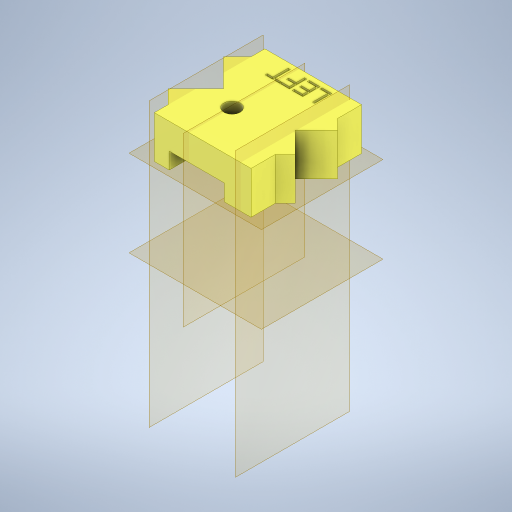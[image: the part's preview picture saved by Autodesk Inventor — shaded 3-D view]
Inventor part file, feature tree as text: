
AUTODESK INVENTOR PART (.ipt)
format: ipt  version: 2023 (Build 270158030, 158C)  size: 1,032,192 bytes
history: native  units: mm
features: sketch x32, extrude x26, projected_geometry x14, hole x7, plane x5, emboss x4, split x3, mirror x2
ambient origin geometry x8: Origin, YZ Plane, XZ Plane, XY Plane, X Axis, Y Axis, Z Axis, Center Point
bodies: Solid1 (feature_tree)
feature tree (93):
  extrude  "MainInnerBodyExtrusion"  Depth=149.0mm
  extrude  "HoleForCamerabase"  Depth=50.0mm
  extrude  "HoleForFan"  Depth=59.0mm
  extrude  "HoleForPi"  TaperAngle=0.0deg  [1 undecoded]
  extrude  "HoleForPoeAdapter"  Depth=62.0mm
  extrude  "HoleForThermister"  Depth=47.0mm
  extrude  "HoleForSensor"  Depth=32.0mm
  extrude  "SlotsForRearFan"  Depth=47.0mm
  extrude  "VentForCamera"  Depth=16.0mm
  extrude  "HoleForLens"  Depth=118.0mm
  sketch  "Sketch23"  dims[d26=49.0mm d27=118.0mm]
  hole  "Hole for 6-32 Insert"  [1 undecoded]
  hole  "Screw hole for 6-32 screw"  [1 undecoded]
  extrude  "Extrusion18"  TaperAngle=0.0deg  [1 undecoded]
  extrude  "HoleForPowerWire"  Depth=17.0mm
  extrude  "Extrusion22"  TaperAngle=0.0deg  [1 undecoded]
  extrude  "Extrusion23"  Depth=2.0mm
  extrude  "ExtrusionForBottom"  Depth=4.0mm
  sketch  "Sketch40"  dims[d46=31.5mm d47=0.0mm]
  plane  "Work Plane1"
  plane  "Work Plane2"
  extrude  "CutOutForFilter"  Depth=4.0mm
  hole  "Hole13"  [1 undecoded]
  plane  "Work Plane4"
  plane  "Work Plane5"
  split  "Split8"
  split  "Split9"
  extrude  "Extrusion35"  Depth=3.0mm
  extrude  "Extrusion36"  Depth=10.0mm
  extrude  "Extrusion37"  Depth=1.5mm
  extrude  "Extrusion38"  Depth=3.0mm
  extrude  "Extrusion to Fix Error"  TaperAngle=0.0deg  [1 undecoded]
  extrude  "Extrusion41"  Depth=15.0mm
  extrude  "Extrusion42"  Depth=5.0mm
  hole  "Hole17"  [1 undecoded]
  hole  "Hole18"  [1 undecoded]
  hole  "Hole19"  [1 undecoded]
  extrude  "Extrusion43"  Depth=1.0mm
  plane  "Work Plane6"
  extrude  "Extrusion44"  Depth=1.0mm
  emboss  "Emboss1"
  emboss  "Emboss2"
  emboss  "Emboss3"
  extrude  "Extrusion45"  Depth=1.0mm
  mirror  "Mirror5"
  hole  "Hole20"  [1 undecoded]
  emboss  "Emboss4"
  mirror  "Mirror6"
  split  "Split11"
  sketch  "Sketch1"  dims[d0=222.7mm d1=149.0mm]
  sketch  "Sketch3"  dims[d2=50.0mm d3=0.0mm d5=15.7mm]
  sketch  "Sketch4"  dims[d6=54.0mm d7=59.0mm]
  sketch  "Sketch6"  dims[d8=47.0mm d9=0.0mm]
  sketch  "Sketch7"  dims[d13=16.0mm d14=62.0mm]
  sketch  "Sketch11"  dims[d15=3.0mm d16=47.0mm]
  sketch  "Sketch15"  dims[d17=0.0mm d20=32.0mm]
  sketch  "Sketch16"  dims[d21=129.0mm d22=47.0mm]
  sketch  "Sketch18"  dims[d23=0.0mm d25=16.0mm]
  sketch  "Sketch25"  dims[d28=47.0mm d29=0.0mm]
  projected_geometry  "Projected Loop1"
  sketch  "Sketch26"  dims[d36=69.0mm d37=28.0mm]
  sketch  "Sketch37"  dims[d38=47.0mm d39=0.0mm]
  projected_geometry  "Projected Loop3"
  projected_geometry  "Projected Loop4"
  sketch  "Sketch39"  dims[d42=50.0mm d43=17.0mm]
  projected_geometry  "Projected Loop5"
  sketch  "Sketch43"  dims[d67=60.0mm d69=2.0mm]
  projected_geometry  "Projected Loop8"
  projected_geometry  "Projected Loop11"
  sketch  "Sketch47"  dims[d71=4.0mm d72=4.0mm]
  projected_geometry  "Projected Loop12"
  sketch  "Sketch51"  dims[d73=4.0mm d75=4.0mm]
  sketch  "Sketch53"  dims[d76=10.0mm d77=0.0mm d78=15.5mm]
  sketch  "Sketch54"  dims[d79=22.0mm d85=3.0mm]
  sketch  "Sketch56"  dims[d86=3.0mm d87=10.0mm]
  projected_geometry  "Projected Loop14"
  sketch  "Sketch57"  dims[d88=16.0mm d89=1.5mm]
  projected_geometry  "Projected Loop15"
  sketch  "Sketch58"  dims[d90=3.0mm d91=3.0mm]
  sketch  "Sketch59"  dims[d92=3.0mm d93=0.0mm d94=0.0mm]
  sketch  "Sketch60"  dims[d95=15.0mm d97=16.0mm]
  sketch  "Sketch62"  dims[d98=10.0mm d99=0.0mm d106=5.0mm]
  projected_geometry  "Projected Loop16"
  sketch  "Sketch63"  dims[d108=5.0mm]
  projected_geometry  "Projected Loop17"
  sketch  "Sketch64"  dims[d109=4.7mm d110=6.0mm d111=5.54mm d112=5.55mm d113=90.0deg d114=7.2mm d115=20.594885mm]
  projected_geometry  "Projected Loop18"
  sketch  "Sketch65"  dims[d116=3.797mm d117=6.0mm d118=12.7mm d119=2.362mm d120=90.0deg d121=15.0mm d122=20.594885mm d137=24.0mm]
  projected_geometry  "Projected Loop19"
  sketch  "Sketch67"  dims[d138=10.0mm d139=3.0mm]
  sketch  "Sketch68"  dims[d140=25.0mm d141=0.0mm d142=30.0mm]
  sketch  "Sketch69"  dims[d144=10.0mm d145=0.0mm d222=76.2mm d223=76.2mm d224=76.2mm d225=76.2mm d228=2.0mm d229=0.0mm d230=2.0mm d231=0.0mm d232=14.0mm d233=0.0mm d234=7.0mm d235=40.0mm d236=40.0mm d246=30.0mm d247=-20.0mm d255=21.0mm d256=52.25mm d257=47.0mm d258=2.25mm d259=0.0mm d264=90.0deg d265=90.0deg d266=90.0deg d267=8.0mm d268=8.0mm d269=8.0mm d270=8.0mm d271=90.0deg d272=90.0deg d273=90.0deg d293=27.0mm d294=5.0mm d295=5.0mm d296=4.699mm d297=6.0mm d298=4.8514mm d299=5.55244mm d300=90.0deg d301=7.1374mm d302=0.0mm d325=149.0mm d326=0.0mm d327=149.0mm d328=0.0mm d329=149.0mm d330=0.0mm d331=0.0mm d332=0.0mm d333=6.0mm d334=7.5mm d335=149.0mm d336=0.0mm d339=149.0mm d340=0.0mm d348=10.0mm d349=0.0mm d350=7.142mm d351=6.0mm d352=12.878mm d353=2.0mm d354=14.3117mm d355=8.0mm d356=0.0mm d357=8.0mm d358=6.0mm d359=9.4mm d360=10.0mm d361=14.3117mm d362=12.7mm d363=0.0mm d364=8.0mm d365=6.0mm d366=9.4mm d367=10.0mm d368=90.0deg d369=12.7mm d370=0.0mm d371=10.0mm d372=0.0mm d373=50.0mm d374=129.0mm d375=0.0mm d376=1.0mm d377=0.0mm d378=1.0mm d379=0.0mm d380=1.0mm d381=0.0mm d382=5.0mm d383=0.0mm d384=20.0mm d385=39.0mm d386=8.0mm d387=6.0mm d388=9.5mm d389=10.0mm d390=90.0deg d391=12.72mm d392=20.594885mm d393=1.0mm d394=0.0mm]
  projected_geometry  "Projected Loop20"
note: 11 required parameter values undecoded (feature->parameter linkage not recoverable at this tier; creation-order binding heuristic only, values carry confidence <= 0.55)
